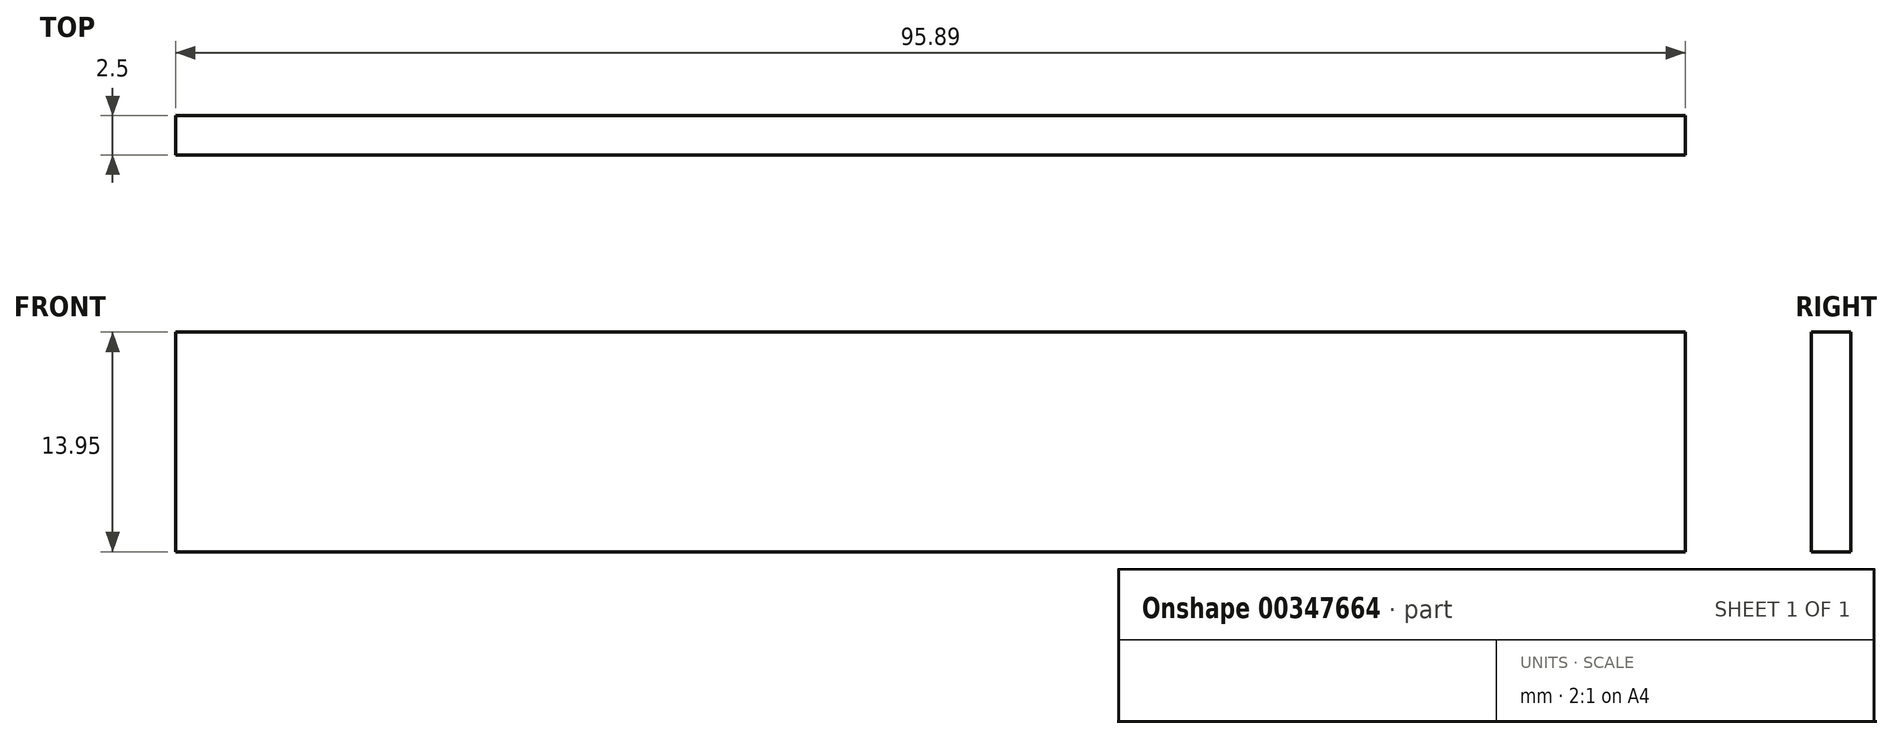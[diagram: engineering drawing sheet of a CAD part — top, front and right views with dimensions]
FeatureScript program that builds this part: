
annotation { "Feature Type Name" : "Feature", "Feature Type Description" : "" }
export const myFeature = defineFeature(function(context is Context, id is Id, definition is map)
    precondition{}
    {
        {
            var Q0;
            Q0=qCreatedBy(makeId("Front.planeOp"),FACE);
            var sketch = newSketch(context, id + "F0", { "sketchPlane" : qUnion([Q0])});
            skLineSegment(sketch, "E0.bottom", {"start": v(-22.46, 10.73) * mm, "end": v(73.43, 10.73) * mm});
            skLineSegment(sketch, "E0.top", {"start": v(-22.46, -3.22) * mm, "end": v(73.43, -3.22) * mm});
            skLineSegment(sketch, "E0.left", {"start": v(-22.46, 10.73) * mm, "end": v(-22.46, -3.22) * mm});
            skLineSegment(sketch, "E0.right", {"start": v(73.43, 10.73) * mm, "end": v(73.43, -3.22) * mm});
            skSolve(sketch);
        }
        {
            var Q0;
            Q0 = qSketchRegion(id + "F0", true);
            extrude(context, id + "F1", {"entities" : qUnion([Q0]), "depth" : 2.5 * mm});
        }
    });
